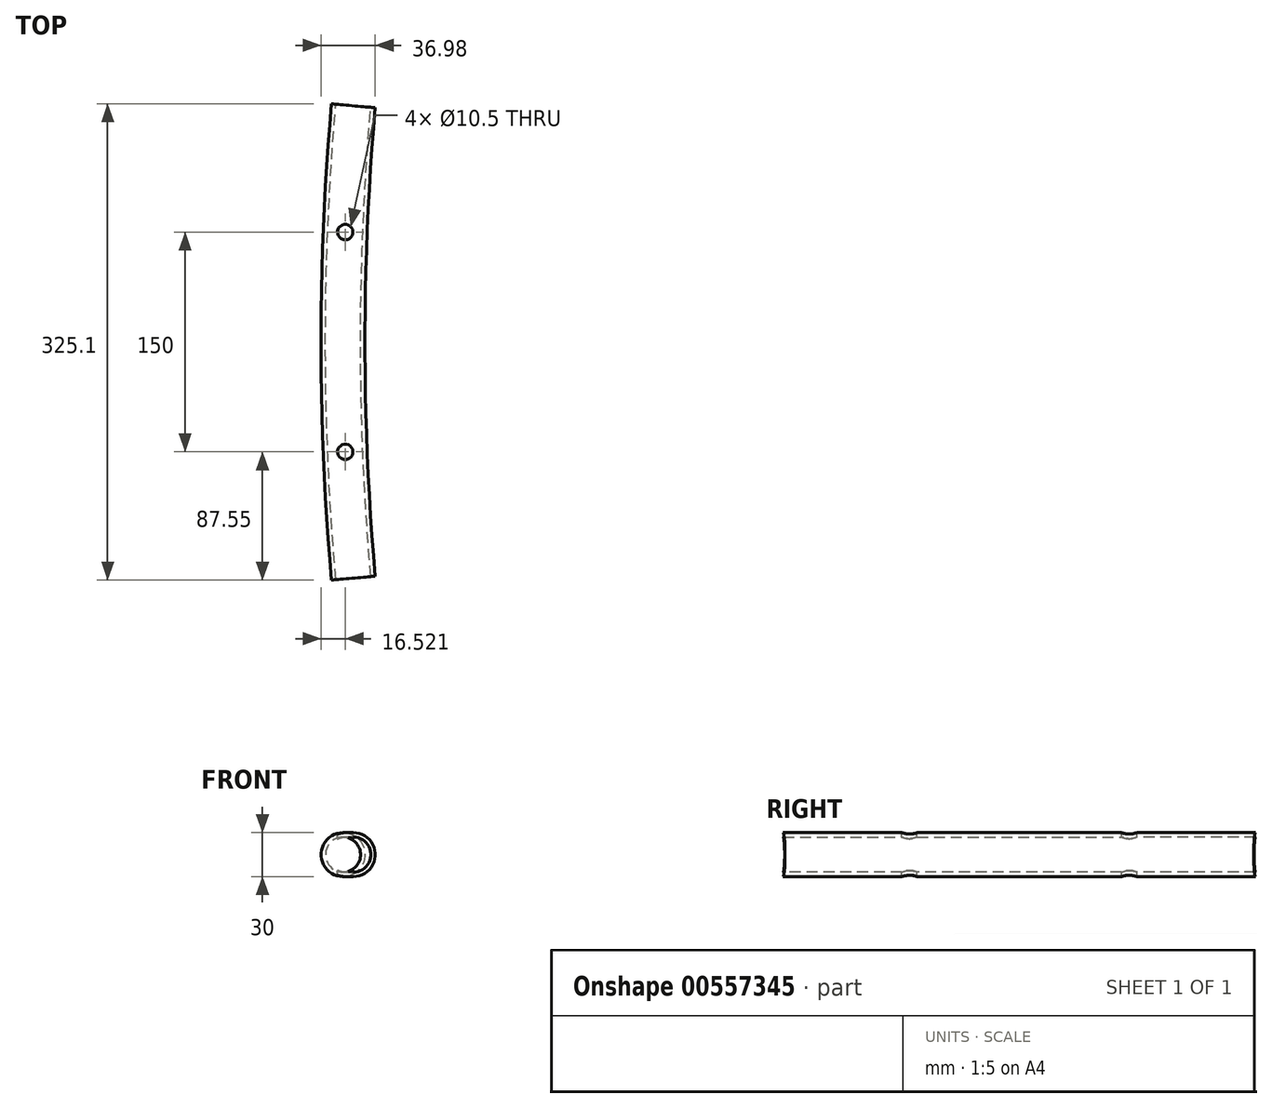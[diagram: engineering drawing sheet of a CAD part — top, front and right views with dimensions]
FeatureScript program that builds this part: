
annotation { "Feature Type Name" : "Feature", "Feature Type Description" : "" }
export const myFeature = defineFeature(function(context is Context, id is Id, definition is map)
    precondition{}
    {
        {
            var Q0;
            Q0=qCreatedBy(makeId("Front.planeOp"),FACE);
            var sketch = newSketch(context, id + "F0", { "sketchPlane" : qUnion([Q0])});
            skCircle(sketch, "E0", {"center": v(-1850, 0) * mm, "radius": 15 * mm});
            skCircle(sketch, "E1", {"center": v(-1850, 0) * mm, "radius": 12 * mm});
            skLineSegment(sketch, "E2", {"start": v(0, 0) * mm, "end": v(0, 380.17) * mm, "construction": true});
            skSolve(sketch);
        }
        {
            var Q0;
            Q0=qSketchRegion(id+"F0",true);
            var Q1;
            Q1=sQuery(id+"F0.wireOp",EDGE,"E2");
            revolve(context, id + "F1", {"entities" : qUnion([Q0]), "axis" : qUnion([Q1]), "revolveType" : RevolveType.SYMMETRIC, "oppositeDirection" : true, "angle" : 10 * degree});
        }
        {
            var Q0;
            Q0=qCreatedBy(makeId("Top.planeOp"),FACE);
            var sketch = newSketch(context, id + "F2", { "sketchPlane" : qUnion([Q0])});
            skArc(sketch, "E3", {"start": v(-1842.96, 161.24) * mm, "mid": v(-1850, 0) * mm, "end": v(-1842.96, -161.24) * mm, "construction": true});
            skCircle(sketch, "E4", {"center": v(-1848.48, -75) * mm, "radius": 5.25 * mm});
            skLineSegment(sketch, "E5", {"start": v(-1850, 0) * mm, "end": v(0, 0) * mm, "construction": true});
            skCircle(sketch, "E6.MirrorC", {"center": v(-1848.48, 75) * mm, "radius": 5.25 * mm});
            skSolve(sketch);
        }
        {
            var Q0;
            Q0=qSketchRegion(id+"F2",true);
            extrude(context, id + "F3", {"entities" : qUnion([Q0]), "operationType" : NewBodyOperationType.REMOVE, "endBound" : BoundingType.THROUGH_ALL, "oppositeDirection" : true, "depth" : 25 * mm, "offsetDistance" : 25 * mm, "hasSecondDirection" : true, "secondDirectionBound" : BoundingType.THROUGH_ALL, "secondDirectionOppositeDirection" : false, "secondDirectionDepth" : 25 * mm});
        }
    });
